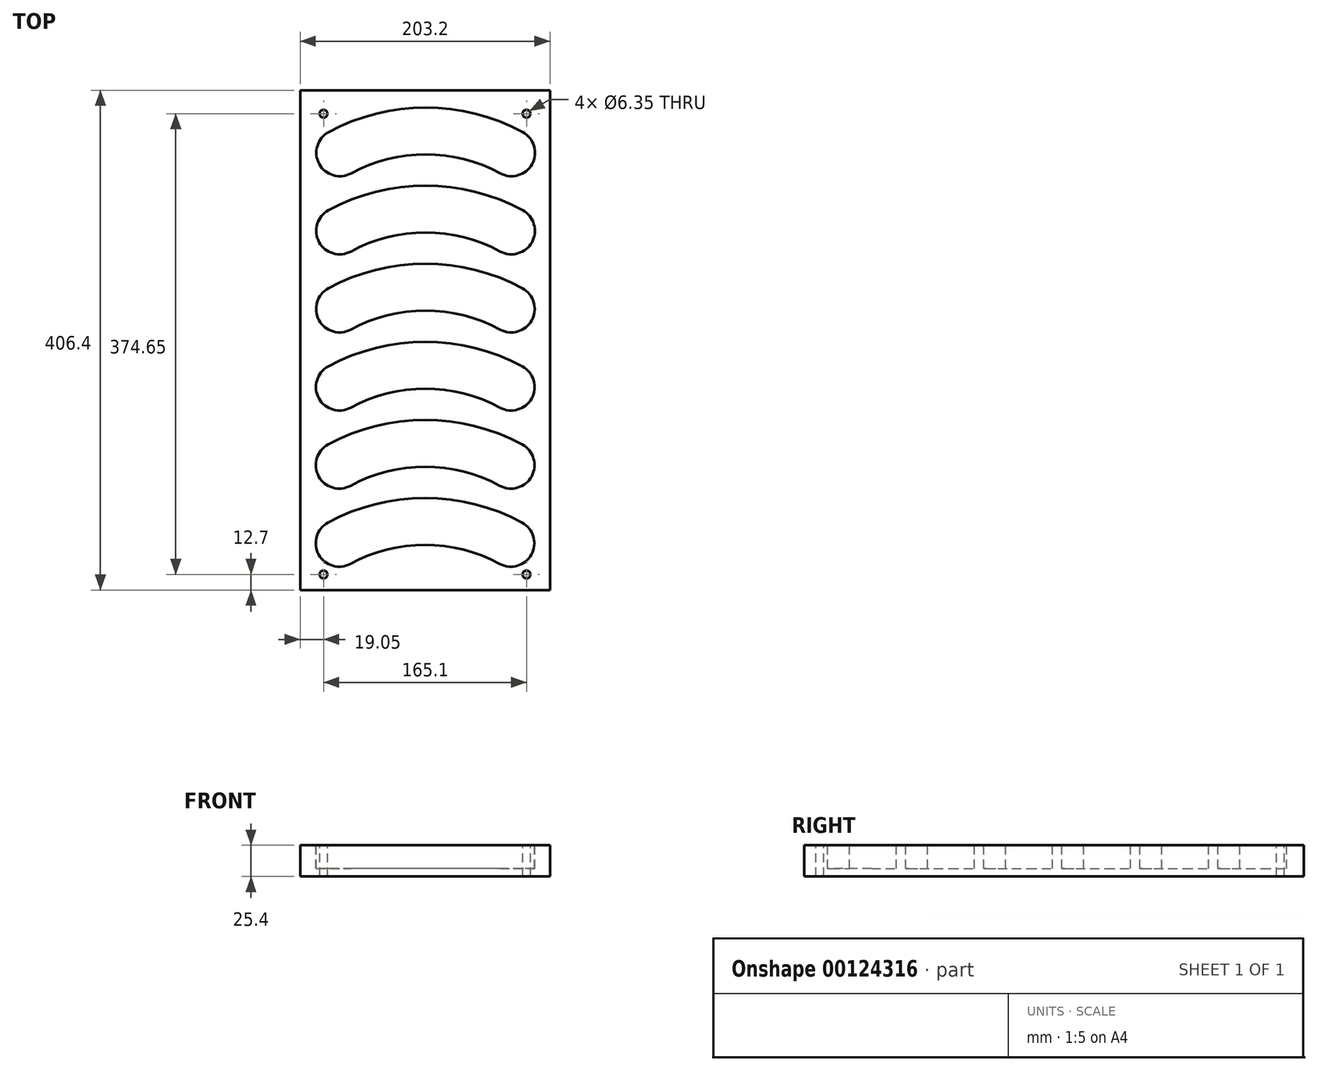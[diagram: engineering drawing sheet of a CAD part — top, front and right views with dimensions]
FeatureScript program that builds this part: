
annotation { "Feature Type Name" : "Feature", "Feature Type Description" : "" }
export const myFeature = defineFeature(function(context is Context, id is Id, definition is map)
    precondition{}
    {
        {
            var Q0;
            Q0=qCreatedBy(makeId("Top.planeOp"),FACE);
            var sketch = newSketch(context, id + "F0", { "sketchPlane" : qUnion([Q0])});
            skLineSegment(sketch, "E0.bottom", {"start": v(0, 0) * mm, "end": v(-203.2, 0) * mm});
            skLineSegment(sketch, "E0.top", {"start": v(0, 406.4) * mm, "end": v(-203.2, 406.4) * mm});
            skLineSegment(sketch, "E0.left", {"start": v(0, 0) * mm, "end": v(0, 406.4) * mm});
            skLineSegment(sketch, "E0.right", {"start": v(-203.2, 0) * mm, "end": v(-203.2, 406.4) * mm});
            skSolve(sketch);
        }
        {
            var Q0;
            Q0 = qSketchRegion(id + "F0", true);
            extrude(context, id + "F1", {"entities" : qUnion([Q0]), "depth" : 25.4 * mm});
        }
        {
            var Q0;
            Q0=makeQuery(id+"F1.opExtrude","CAP_FACE",FACE,{"disambiguationData":[OSD([sQuery(id+"F0.wireOp",EDGE,"E0.bottom"),sQuery(id+"F0.wireOp",EDGE,"E0.top"),sQuery(id+"F0.wireOp",EDGE,"E0.left"),sQuery(id+"F0.wireOp",EDGE,"E0.right")])],"isStart":false});
            var sketch = newSketch(context, id + "F2", { "sketchPlane" : qUnion([Q0])});
            skArc(sketch, "E1", {"start": v(-40.86, 21.37) * mm, "mid": v(-101.6, 36.84) * mm, "end": v(-162.34, 21.37) * mm});
            skArc(sketch, "E2", {"start": v(-22.64, 54.83) * mm, "mid": v(-101.6, 74.94) * mm, "end": v(-180.56, 54.83) * mm});
            skPoint(sketch, "E2.startSnap0", {"position": v(-101.6, 36.84) * mm});
            skArc(sketch, "E3", {"start": v(-180.56, 54.83) * mm, "mid": v(-188.18, 28.99) * mm, "end": v(-162.34, 21.37) * mm});
            skPoint(sketch, "E4", {"position": v(-101.6, 406.4) * mm});
            skArc(sketch, "E5", {"start": v(-40.86, 21.37) * mm, "mid": v(-15.02, 28.99) * mm, "end": v(-22.64, 54.83) * mm});
            skLineSegment(sketch, "E6", {"start": v(-162.34, 21.37) * mm, "end": v(-171.45, 38.1) * mm, "construction": true});
            skLineSegment(sketch, "E7", {"start": v(-162.34, 21.37) * mm, "end": v(-180.56, 54.83) * mm, "construction": true});
            skLineSegment(sketch, "E8", {"start": v(-40.86, 21.37) * mm, "end": v(-22.64, 54.83) * mm, "construction": true});
            skPoint(sketch, "E9", {"position": v(-101.6, 74.94) * mm});
            skArc(sketch, "E10.0.1.0", {"start": v(-40.75, 84.87) * mm, "mid": v(-14.91, 92.49) * mm, "end": v(-22.53, 118.33) * mm});
            skArc(sketch, "E10.0.1.1", {"start": v(-180.45, 118.33) * mm, "mid": v(-188.07, 92.49) * mm, "end": v(-162.23, 84.87) * mm});
            skArc(sketch, "E10.0.1.2", {"start": v(-22.53, 118.33) * mm, "mid": v(-101.5, 138.44) * mm, "end": v(-180.45, 118.33) * mm});
            skArc(sketch, "E10.0.1.3", {"start": v(-40.75, 84.87) * mm, "mid": v(-101.5, 100.34) * mm, "end": v(-162.23, 84.87) * mm});
            skPoint(sketch, "E10.0.1.4", {"position": v(-101.5, 100.34) * mm});
            skPoint(sketch, "E10.0.1.5", {"position": v(-101.5, 138.44) * mm});
            skLineSegment(sketch, "E10.0.1.6", {"start": v(-40.75, 84.87) * mm, "end": v(-22.53, 118.33) * mm, "construction": true});
            skLineSegment(sketch, "E10.0.1.7", {"start": v(-162.23, 84.87) * mm, "end": v(-171.34, 101.6) * mm, "construction": true});
            skLineSegment(sketch, "E10.0.1.8", {"start": v(-162.23, 84.87) * mm, "end": v(-180.45, 118.33) * mm, "construction": true});
            skArc(sketch, "E10.0.2.0", {"start": v(-40.65, 148.37) * mm, "mid": v(-14.8, 155.99) * mm, "end": v(-22.43, 181.83) * mm});
            skArc(sketch, "E10.0.2.1", {"start": v(-180.35, 181.83) * mm, "mid": v(-187.97, 155.99) * mm, "end": v(-162.13, 148.37) * mm});
            skArc(sketch, "E10.0.2.2", {"start": v(-22.43, 181.83) * mm, "mid": v(-101.39, 201.94) * mm, "end": v(-180.35, 181.83) * mm});
            skArc(sketch, "E10.0.2.3", {"start": v(-40.65, 148.37) * mm, "mid": v(-101.39, 163.84) * mm, "end": v(-162.13, 148.37) * mm});
            skPoint(sketch, "E10.0.2.4", {"position": v(-101.39, 163.84) * mm});
            skPoint(sketch, "E10.0.2.5", {"position": v(-101.39, 201.94) * mm});
            skLineSegment(sketch, "E10.0.2.6", {"start": v(-40.65, 148.37) * mm, "end": v(-22.43, 181.83) * mm, "construction": true});
            skLineSegment(sketch, "E10.0.2.7", {"start": v(-162.13, 148.37) * mm, "end": v(-171.24, 165.1) * mm, "construction": true});
            skLineSegment(sketch, "E10.0.2.8", {"start": v(-162.13, 148.37) * mm, "end": v(-180.35, 181.83) * mm, "construction": true});
            skArc(sketch, "E10.0.3.0", {"start": v(-40.54, 211.87) * mm, "mid": v(-14.7, 219.49) * mm, "end": v(-22.32, 245.33) * mm});
            skArc(sketch, "E10.0.3.1", {"start": v(-180.24, 245.33) * mm, "mid": v(-187.86, 219.49) * mm, "end": v(-162.02, 211.87) * mm});
            skArc(sketch, "E10.0.3.2", {"start": v(-22.32, 245.33) * mm, "mid": v(-101.28, 265.44) * mm, "end": v(-180.24, 245.33) * mm});
            skArc(sketch, "E10.0.3.3", {"start": v(-40.54, 211.87) * mm, "mid": v(-101.28, 227.34) * mm, "end": v(-162.02, 211.87) * mm});
            skPoint(sketch, "E10.0.3.4", {"position": v(-101.28, 227.34) * mm});
            skPoint(sketch, "E10.0.3.5", {"position": v(-101.28, 265.44) * mm});
            skLineSegment(sketch, "E10.0.3.6", {"start": v(-40.54, 211.87) * mm, "end": v(-22.32, 245.33) * mm, "construction": true});
            skLineSegment(sketch, "E10.0.3.7", {"start": v(-162.02, 211.87) * mm, "end": v(-171.13, 228.6) * mm, "construction": true});
            skLineSegment(sketch, "E10.0.3.8", {"start": v(-162.02, 211.87) * mm, "end": v(-180.24, 245.33) * mm, "construction": true});
            skArc(sketch, "E10.0.4.0", {"start": v(-40.44, 275.37) * mm, "mid": v(-14.6, 282.99) * mm, "end": v(-22.21, 308.83) * mm});
            skArc(sketch, "E10.0.4.1", {"start": v(-180.14, 308.83) * mm, "mid": v(-187.76, 282.99) * mm, "end": v(-161.91, 275.37) * mm});
            skArc(sketch, "E10.0.4.2", {"start": v(-22.21, 308.83) * mm, "mid": v(-101.18, 328.94) * mm, "end": v(-180.14, 308.83) * mm});
            skArc(sketch, "E10.0.4.3", {"start": v(-40.44, 275.37) * mm, "mid": v(-101.18, 290.84) * mm, "end": v(-161.91, 275.37) * mm});
            skPoint(sketch, "E10.0.4.4", {"position": v(-101.18, 290.84) * mm});
            skPoint(sketch, "E10.0.4.5", {"position": v(-101.18, 328.94) * mm});
            skLineSegment(sketch, "E10.0.4.6", {"start": v(-40.44, 275.37) * mm, "end": v(-22.21, 308.83) * mm, "construction": true});
            skLineSegment(sketch, "E10.0.4.7", {"start": v(-161.91, 275.37) * mm, "end": v(-171.03, 292.1) * mm, "construction": true});
            skLineSegment(sketch, "E10.0.4.8", {"start": v(-161.91, 275.37) * mm, "end": v(-180.14, 308.83) * mm, "construction": true});
            skArc(sketch, "E10.0.5.0", {"start": v(-40.33, 338.87) * mm, "mid": v(-14.49, 346.49) * mm, "end": v(-22.1, 372.33) * mm});
            skArc(sketch, "E10.0.5.1", {"start": v(-180.03, 372.33) * mm, "mid": v(-187.65, 346.49) * mm, "end": v(-161.8, 338.87) * mm});
            skArc(sketch, "E10.0.5.2", {"start": v(-22.1, 372.33) * mm, "mid": v(-101.07, 392.44) * mm, "end": v(-180.03, 372.33) * mm});
            skArc(sketch, "E10.0.5.3", {"start": v(-40.33, 338.87) * mm, "mid": v(-101.07, 354.34) * mm, "end": v(-161.8, 338.87) * mm});
            skPoint(sketch, "E10.0.5.4", {"position": v(-101.07, 354.34) * mm});
            skPoint(sketch, "E10.0.5.5", {"position": v(-101.07, 392.44) * mm});
            skLineSegment(sketch, "E10.0.5.6", {"start": v(-40.33, 338.87) * mm, "end": v(-22.1, 372.33) * mm, "construction": true});
            skLineSegment(sketch, "E10.0.5.7", {"start": v(-161.8, 338.87) * mm, "end": v(-170.92, 355.6) * mm, "construction": true});
            skLineSegment(sketch, "E10.0.5.8", {"start": v(-161.8, 338.87) * mm, "end": v(-180.03, 372.33) * mm, "construction": true});
            skLineSegment(sketch, "E10.direction1", {"start": v(-101.6, 36.84) * mm, "end": v(-102.74, 36.86) * mm, "construction": true});
            skLineSegment(sketch, "E10.direction2", {"start": v(-101.6, 36.84) * mm, "end": v(-101.5, 100.34) * mm, "construction": true});
            skSolve(sketch);
        }
        {
            var Q0;
            Q0 = qSketchRegion(id + "F2", true);
            extrude(context, id + "F3", {"entities" : qUnion([Q0]), "operationType" : NewBodyOperationType.REMOVE, "oppositeDirection" : true, "depth" : 19.05 * mm});
        }
        {
            var Q0;
            Q0=makeQuery(id+"F1.opExtrude","CAP_FACE",FACE,{"disambiguationData":[OSD([sQuery(id+"F0.wireOp",EDGE,"E0.bottom"),sQuery(id+"F0.wireOp",EDGE,"E0.top"),sQuery(id+"F0.wireOp",EDGE,"E0.left"),sQuery(id+"F0.wireOp",EDGE,"E0.right")])],"isStart":false});
            var sketch = newSketch(context, id + "F4", { "sketchPlane" : qUnion([Q0])});
            skCircle(sketch, "E11", {"center": v(-184.15, 387.35) * mm, "radius": 3.18 * mm});
            skCircle(sketch, "E12", {"center": v(-19.05, 387.35) * mm, "radius": 3.18 * mm});
            skCircle(sketch, "E13", {"center": v(-184.15, 12.7) * mm, "radius": 3.18 * mm});
            skCircle(sketch, "E14", {"center": v(-19.05, 12.7) * mm, "radius": 3.18 * mm});
            skSolve(sketch);
        }
        {
            var Q0;
            Q0 = qSketchRegion(id + "F4", true);
            extrude(context, id + "F5", {"entities" : qUnion([Q0]), "operationType" : NewBodyOperationType.REMOVE, "endBound" : BoundingType.THROUGH_ALL, "oppositeDirection" : true, "depth" : 25.4 * mm});
        }
    });
